# Revit family: P560274-031
name_source: partatom
category: Lighting Fixtures
revit_build: Autodesk Revit 2014 (Build: 20130308_1515(x64)
units: mm (PartAtom-declared; Revit-internal decimal feet)

## types (1)
- P560274-031
    Apparent Load = 100 VA
    Assembly Code = D5020200
    Color Filter = 16777215
    Connector Description = Lighting Connector
    Default Elevation = 48 "
    Description = Exton Collection One-Light Textured Black and Etched Seeded Glass Modern Style Large Outdoor Wall Lantern
    Dimming Lamp Color Temperature Shift = <None>
    Features = Application: Architectural influences blend harmoniously in the Exton Collection 1-Light Textured Black Etched Glass Modern Large Wall Lantern Light ideal for any covered porch, patio, deck, and foyer.
Styles: Perfect for modern and contemporary style settings.
Finish: The clean lines and geometric forms interact in the textured black frame culminating in an iconic peaked roof.
Materials: Constructed from steel to ensure a long product lifespan.
Glass/Shades: A light source glows from within an etched glass shade that accentuates the lantern's contemporary aesthetic.
Bulbs: For ideal illumination, use 1 medium base bulb that is sold separately (100w max - LED/CFL/incandescent)
compatible with dimmable bulbs.
Dimensions: Measures 11-1/8-inch diameter by 15-1/2-inch height.
Certifications: cCSAus wet location listed.
Pairs With: Pairs with a variety of Progress Lighting fixtures.
Warranty: Our 1-Year Limited Warranty guarantees your complete satisfaction with your purchase and includes professional after-sales customer service support.
    Fixture distribution = Direct
    Glass = Paint - Hubbell - White Texture
    Gold = Hubbell - Gold
    Housing Material = Paint - Hubbell - Textured Camera Black
    Lamp = LED/CFL/incandescent
    Load Classification = Lighting
    Manufacturer = Progress Lighting
    Model = P560274-031
    Photometric Web File = generic
    Power Factor = 1
    Product Documentation Link = https://hubbellcdn.com
    Product Link = https://www.hubbell.com
    Steel = Paint - Hubbell - Stainless Stell
    Support = Paint - Hubbell - Stainless Stell
    Tilt Angle = 60.00°
    URL = https://www.hubbell.com
    Voltage = 120 V
    Warranty = 1 year Warranty
    Wattage Comments = 100W
    Watts = 100 W

## geometry (parser evidence)
native form markers: Sweep x6
no freeform markers — native parametric forms only
